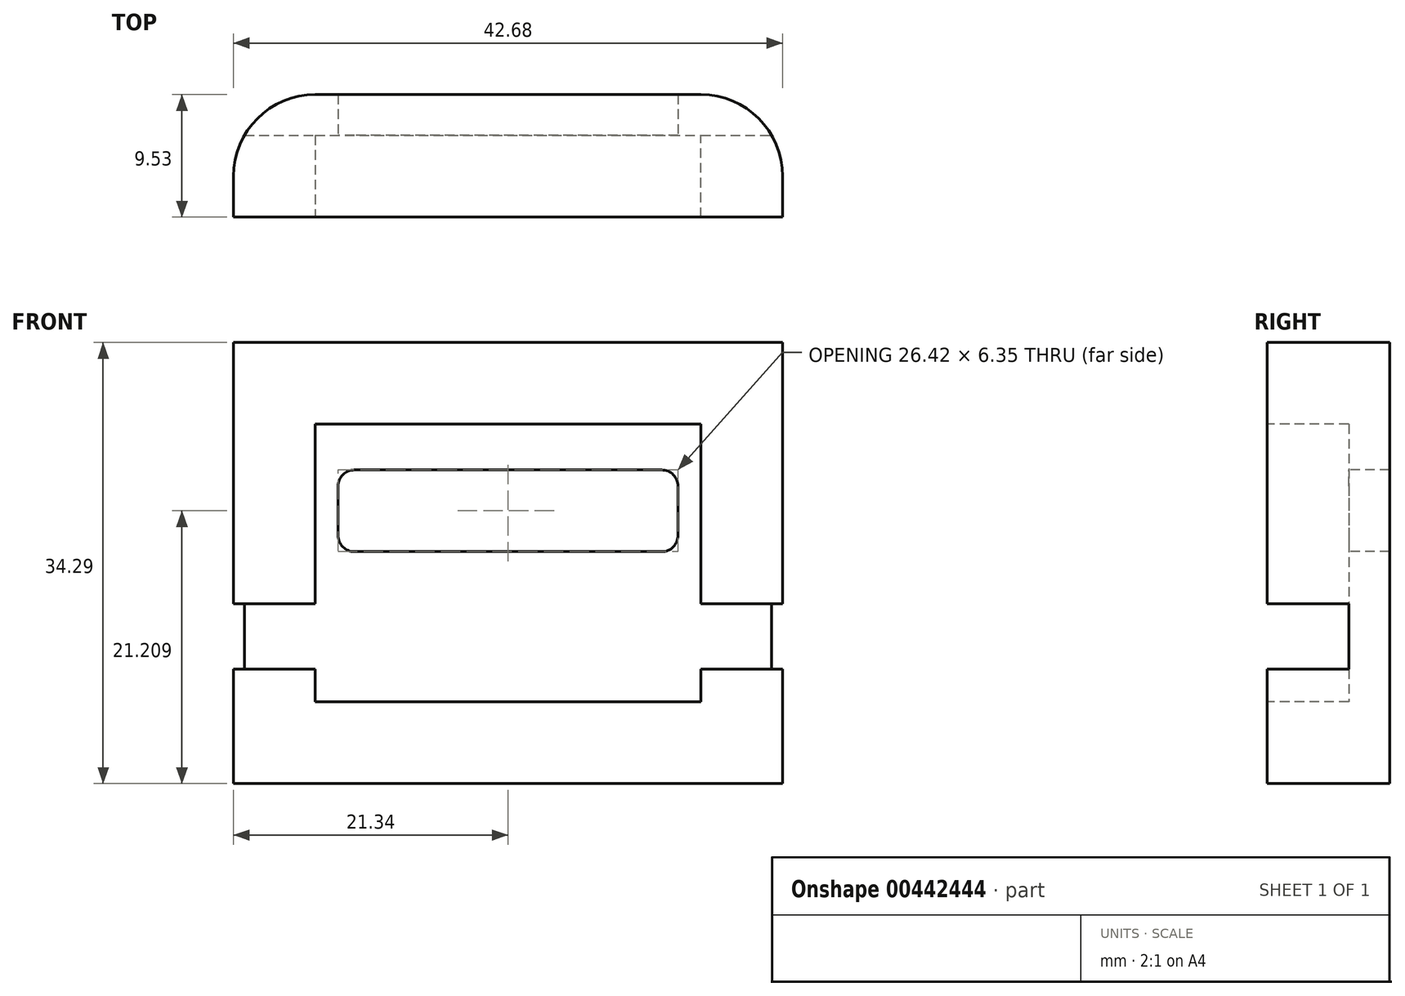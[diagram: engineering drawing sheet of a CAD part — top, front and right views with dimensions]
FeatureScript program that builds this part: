
annotation { "Feature Type Name" : "Feature", "Feature Type Description" : "" }
export const myFeature = defineFeature(function(context is Context, id is Id, definition is map)
    precondition{}
    {
        {
            var Q0;
            Q0=qCreatedBy(makeId("Top.planeOp"),FACE);
            var sketch = newSketch(context, id + "F0", { "sketchPlane" : qUnion([Q0])});
            skLineSegment(sketch, "E0.bottom", {"start": v(-14.35, -3.17) * mm, "end": v(14.35, -3.18) * mm, "construction": true});
            skLineSegment(sketch, "E0.top", {"start": v(-14.35, 3.18) * mm, "end": v(14.35, 3.17) * mm, "construction": true});
            skLineSegment(sketch, "E0.left", {"start": v(-14.35, -3.17) * mm, "end": v(-14.35, 3.17) * mm, "construction": true});
            skLineSegment(sketch, "E0.right", {"start": v(14.35, -3.17) * mm, "end": v(14.35, 3.17) * mm, "construction": true});
            skLineSegment(sketch, "E1", {"start": v(-14.99, -3.18) * mm, "end": v(-14.99, 3.17) * mm});
            skLineSegment(sketch, "E2", {"start": v(-14.99, 3.18) * mm, "end": v(14.99, 3.18) * mm});
            skLineSegment(sketch, "E3", {"start": v(14.99, 3.17) * mm, "end": v(14.99, -3.18) * mm});
            skLineSegment(sketch, "E4", {"start": v(14.99, -3.18) * mm, "end": v(21.34, -3.18) * mm});
            skLineSegment(sketch, "E5", {"start": v(21.34, -3.18) * mm, "end": v(21.34, 0) * mm});
            skLineSegment(sketch, "E6", {"start": v(14.99, 6.35) * mm, "end": v(-14.99, 6.35) * mm});
            skLineSegment(sketch, "E7", {"start": v(-21.34, 0) * mm, "end": v(-21.34, -3.18) * mm});
            skLineSegment(sketch, "E8", {"start": v(-21.34, -3.18) * mm, "end": v(-14.99, -3.18) * mm});
            skPoint(sketch, "E9.visualSharp", {"position": v(-21.34, 6.35) * mm});
            skArc(sketch, "E9.filletArc", {"start": v(-14.99, 6.35) * mm, "mid": v(-19.48, 4.5) * mm, "end": v(-21.34, 0) * mm});
            skPoint(sketch, "E10.visualSharp", {"position": v(21.34, 6.35) * mm});
            skArc(sketch, "E10.filletArc", {"start": v(21.34, 0) * mm, "mid": v(19.48, 4.5) * mm, "end": v(14.99, 6.35) * mm});
            skSolve(sketch);
        }
        {
            var Q0;
            Q0=makeQuery(id+"F0.imprint","IMPRINT",FACE,{"disambiguationData":[TD([[makeQuery(id+"F0.imprint","IMPRINT",EDGE,{"derivedFrom":sQuery(id+"F0.wireOp",EDGE,"E1")}),1.0]])]});
            extrude(context, id + "F1", {"entities" : qUnion([Q0]), "depth" : 34.3 * mm});
        }
        {
            var Q0;
            Q0=makeQuery(id+"F1.opExtrude","SWEPT_FACE",FACE,{"disambiguationData":[OSD([sQuery(id+"F0.wireOp",EDGE,"E8")])]});
            var sketch = newSketch(context, id + "F2", { "sketchPlane" : qUnion([Q0])});
            skLineSegment(sketch, "E11.bottom", {"start": v(-14.99, 0) * mm, "end": v(14.99, 0) * mm});
            skLineSegment(sketch, "E11.top", {"start": v(-14.99, 6.35) * mm, "end": v(14.99, 6.35) * mm});
            skLineSegment(sketch, "E11.left", {"start": v(-14.99, 0) * mm, "end": v(-14.99, 6.35) * mm});
            skLineSegment(sketch, "E11.right", {"start": v(14.99, 0) * mm, "end": v(14.99, 6.35) * mm});
            skLineSegment(sketch, "E12.bottom", {"start": v(-14.99, 27.94) * mm, "end": v(14.99, 27.94) * mm});
            skLineSegment(sketch, "E12.top", {"start": v(-14.99, 34.3) * mm, "end": v(14.99, 34.3) * mm});
            skLineSegment(sketch, "E12.left", {"start": v(-14.99, 27.94) * mm, "end": v(-14.99, 34.3) * mm});
            skLineSegment(sketch, "E12.right", {"start": v(14.99, 27.94) * mm, "end": v(14.99, 34.3) * mm});
            skLineSegment(sketch, "E13.bottom", {"start": v(-21.34, 8.89) * mm, "end": v(21.34, 8.89) * mm});
            skLineSegment(sketch, "E13.top", {"start": v(-21.34, 13.97) * mm, "end": v(21.34, 13.97) * mm});
            skLineSegment(sketch, "E13.left", {"start": v(-21.34, 8.89) * mm, "end": v(-21.34, 13.97) * mm});
            skLineSegment(sketch, "E13.right", {"start": v(21.34, 8.89) * mm, "end": v(21.34, 13.97) * mm});
            skLineSegment(sketch, "E14", {"start": v(-21.34, 11.43) * mm, "end": v(21.34, 11.43) * mm, "construction": true});
            skLineSegment(sketch, "E15.bottom", {"start": v(-11.94, 18.03) * mm, "end": v(11.94, 18.03) * mm});
            skLineSegment(sketch, "E15.top", {"start": v(-11.94, 24.38) * mm, "end": v(11.94, 24.38) * mm});
            skLineSegment(sketch, "E15.left", {"start": v(-13.2, 19.3) * mm, "end": v(-13.2, 23.11) * mm});
            skLineSegment(sketch, "E15.right", {"start": v(13.2, 19.3) * mm, "end": v(13.2, 23.11) * mm});
            skLineSegment(sketch, "E16", {"start": v(-21.34, 21.2) * mm, "end": v(21.34, 21.2) * mm, "construction": true});
            skPoint(sketch, "E17.visualSharp", {"position": v(-13.2, 24.38) * mm});
            skArc(sketch, "E17.filletArc", {"start": v(-11.94, 24.38) * mm, "mid": v(-12.84, 24.01) * mm, "end": v(-13.2, 23.11) * mm});
            skPoint(sketch, "E18.visualSharp", {"position": v(13.2, 24.38) * mm});
            skArc(sketch, "E18.filletArc", {"start": v(13.2, 23.11) * mm, "mid": v(12.84, 24.01) * mm, "end": v(11.94, 24.38) * mm});
            skPoint(sketch, "E19.visualSharp", {"position": v(13.2, 18.03) * mm});
            skArc(sketch, "E19.filletArc", {"start": v(11.94, 18.03) * mm, "mid": v(12.84, 18.4) * mm, "end": v(13.2, 19.3) * mm});
            skPoint(sketch, "E20.visualSharp", {"position": v(-13.2, 18.03) * mm});
            skArc(sketch, "E20.filletArc", {"start": v(-13.2, 19.3) * mm, "mid": v(-12.84, 18.4) * mm, "end": v(-11.94, 18.03) * mm});
            skLineSegment(sketch, "E21", {"start": v(0, 20.18) * mm, "end": v(0, 15.64) * mm});
            skLineSegment(sketch, "E22", {"start": v(-2.3, 17.15) * mm, "end": v(2.65, 17.15) * mm});
            skPoint(sketch, "E23", {"position": v(0, 17.15) * mm});
            skSolve(sketch);
        }
        {
            var Q0;
            Q0=makeQuery(id+"F2.imprint","IMPRINT",FACE,{"disambiguationData":[TD([[makeQuery(id+"F2.imprint","IMPRINT",EDGE,{"derivedFrom":sQuery(id+"F2.wireOp",EDGE,"E11.bottom")}),1.0]])]});
            var Q1;
            Q1=makeQuery(id+"F2.imprint","IMPRINT",FACE,{"disambiguationData":[TD([[makeQuery(id+"F2.imprint","IMPRINT",EDGE,{"derivedFrom":sQuery(id+"F2.wireOp",EDGE,"E12.bottom")}),1.0]])]});
            var Q2;
            Q2=makeQuery(id+"F1.opExtrude","SWEPT_FACE",FACE,{"disambiguationData":[OSD([sQuery(id+"F0.wireOp",EDGE,"E2")])]});
            extrude(context, id + "F3", {"entities" : qUnion([Q0, Q1]), "operationType" : NewBodyOperationType.ADD, "endBound" : BoundingType.UP_TO_SURFACE, "oppositeDirection" : true, "endBoundEntityFace" : qUnion([Q2]), "depth" : 3.35 * mm});
        }
        {
            var Q0;
            {var subQ0=sQuery(id+"F2.wireOp",EDGE,"E13.left");Q0=makeQuery(id+"F2.imprint","IMPRINT",FACE,{"disambiguationData":[TD([[makeQuery(id+"F2.imprint","IMPRINT",EDGE,{"derivedFrom":subQ0}),1.0]])]});}
            var Q1;
            {var subQ0=sQuery(id+"F2.wireOp",EDGE,"E13.right");Q1=makeQuery(id+"F2.imprint","IMPRINT",FACE,{"disambiguationData":[TD([[makeQuery(id+"F2.imprint","IMPRINT",EDGE,{"derivedFrom":subQ0}),1.0]])]});}
            var Q2;
            Q2=makeQuery(id+"F3.boolean.opBoolean","SPLIT",FACE,{"disambiguationData":[TD([makeQuery(id+"F3.opExtrude","SWEPT_FACE",FACE,{"disambiguationData":[OSD([sQuery(id+"F2.wireOp",EDGE,"E11.top")])]})])],"derivedFrom":makeQuery(id+"F1.opExtrude","SWEPT_FACE",FACE,{"disambiguationData":[OSD([sQuery(id+"F0.wireOp",EDGE,"E2")])]})});
            extrude(context, id + "F4", {"entities" : qUnion([Q0, Q1]), "operationType" : NewBodyOperationType.REMOVE, "endBound" : BoundingType.UP_TO_SURFACE, "oppositeDirection" : true, "endBoundEntityFace" : qUnion([Q2]), "depth" : 2.03 * mm});
        }
        {
            var Q0;
            Q0=makeQuery(id+"F2.imprint","IMPRINT",FACE,{"disambiguationData":[TD([[makeQuery(id+"F2.imprint","IMPRINT",EDGE,{"derivedFrom":sQuery(id+"F2.wireOp",EDGE,"E15.bottom")}),1.0]])]});
            extrude(context, id + "F5", {"entities" : qUnion([Q0]), "operationType" : NewBodyOperationType.REMOVE, "endBound" : BoundingType.THROUGH_ALL, "oppositeDirection" : true, "depth" : 25.4 * mm});
        }
    });
